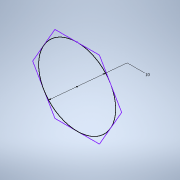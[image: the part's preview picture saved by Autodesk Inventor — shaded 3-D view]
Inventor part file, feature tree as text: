
AUTODESK INVENTOR PART (.ipt)
format: ipt  version: 2020 (Build 240168000, 168)  size: 113,152 bytes
history: native  units: mm
features: extrude x2, sketch x2, thread x1, fillet x1
ambient origin geometry x8: Origin, YZ Plane, XZ Plane, XY Plane, X Axis, Y Axis, Z Axis, Center Point
bodies: Solido1 (feature_tree)
feature tree (6):
  extrude  "Estrusione1"  Depth=10.0mm
  extrude  "Estrusione2"  Depth=4.0mm TaperAngle=0.0deg
  thread  "Filettatura1"
  fillet  "Raccordo1"  Radius=6.0mm
  sketch  "Schizzo1"
  sketch  "Schizzo3"
